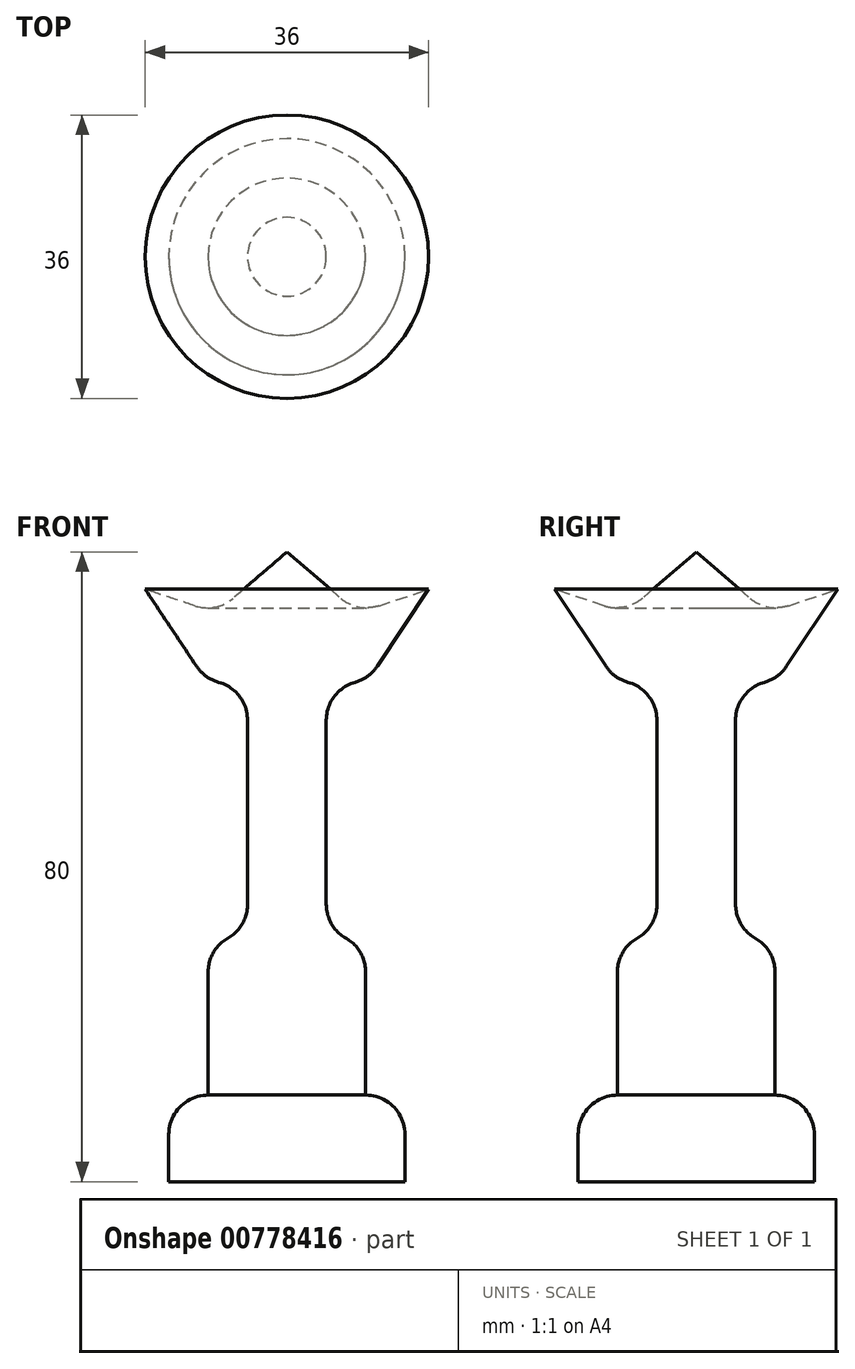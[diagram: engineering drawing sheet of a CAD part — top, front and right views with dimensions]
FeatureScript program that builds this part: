
annotation { "Feature Type Name" : "Feature", "Feature Type Description" : "" }
export const myFeature = defineFeature(function(context is Context, id is Id, definition is map)
    precondition{}
    {
        {
            var Q0;
            Q0=qCreatedBy(makeId("Front.planeOp"),FACE);
            var sketch = newSketch(context, id + "F0", { "sketchPlane" : qUnion([Q0])});
            skLineSegment(sketch, "E0", {"start": v(0, -7.82) * mm, "end": v(0, 61.44) * mm});
            skLineSegment(sketch, "E1", {"start": v(5, 55.44) * mm, "end": v(10, 55.44) * mm});
            skLineSegment(sketch, "E2", {"start": v(10, 55.44) * mm, "end": v(18, 67.44) * mm});
            skLineSegment(sketch, "E3", {"start": v(18, 67.44) * mm, "end": v(9, 64.44) * mm});
            skLineSegment(sketch, "E4", {"start": v(0, 61.44) * mm, "end": v(0, 55.44) * mm});
            skLineSegment(sketch, "E5", {"start": v(0, -7.82) * mm, "end": v(15, -7.82) * mm});
            skLineSegment(sketch, "E6", {"start": v(15, -7.82) * mm, "end": v(15, 3.18) * mm});
            skLineSegment(sketch, "E7", {"start": v(15, 3.18) * mm, "end": v(10, 3.18) * mm});
            skLineSegment(sketch, "E8", {"start": v(10, 3.18) * mm, "end": v(10, 23.7) * mm});
            skLineSegment(sketch, "E9", {"start": v(10, 23.7) * mm, "end": v(5, 23.7) * mm});
            skLineSegment(sketch, "E10", {"start": v(5, 23.7) * mm, "end": v(5, 55.44) * mm});
            skPoint(sketch, "E11.orphan", {"position": v(0, 23.7) * mm});
            skPoint(sketch, "E12.orphan", {"position": v(0, 3.18) * mm});
            skPoint(sketch, "E13.orphan", {"position": v(0, 72.18) * mm});
            skLineSegment(sketch, "E14", {"start": v(0, 61.44) * mm, "end": v(0, 72.18) * mm});
            skLineSegment(sketch, "E15", {"start": v(0, 72.18) * mm, "end": v(9, 64.44) * mm});
            skSolve(sketch);
        }
        {
            var Q0;
            Q0=makeQuery(id+"F0.imprint","IMPRINT",FACE,{"disambiguationData":[TD([[makeQuery(id+"F0.imprint","IMPRINT",EDGE,{"derivedFrom":sQuery(id+"F0.wireOp",EDGE,"E0")}),-1.0]])]});
            var Q1;
            Q1=sQuery(id+"F0.wireOp",EDGE,"E0");
            revolve(context, id + "F1", {"surfaceOperationType" : NewSurfaceOperationType.NEW, "entities" : qUnion([Q0]), "axis" : qUnion([Q1]), "revolveType" : RevolveType.FULL});
        }
        {
            var Q0;
            Q0=makeQuery(id+"F1.opRevolve","SWEPT_EDGE",EDGE,{"disambiguationData":[OSD([sQuery(id+"F0.wireOp",EDGE,"E8"),sQuery(id+"F0.wireOp",EDGE,"E9")])]});
            fillet(context, id + "F2", {"entities" : qUnion([Q0]), "radius" : 4.83 * mm, "tangentPropagation" : true, "allowEdgeOverflow" : false});
        }
        {
            var Q0;
            Q0=makeQuery(id+"F1.opRevolve","SWEPT_EDGE",EDGE,{"disambiguationData":[OSD([sQuery(id+"F0.wireOp",EDGE,"E6"),sQuery(id+"F0.wireOp",EDGE,"E7")])]});
            fillet(context, id + "F3", {"entities" : qUnion([Q0]), "radius" : 5 * mm, "tangentPropagation" : true, "allowEdgeOverflow" : false});
        }
        {
            var Q0;
            Q0=makeQuery(id+"F1.opRevolve","SWEPT_EDGE",EDGE,{"disambiguationData":[OSD([sQuery(id+"F0.wireOp",EDGE,"E9"),sQuery(id+"F0.wireOp",EDGE,"E10")])]});
            fillet(context, id + "F4", {"entities" : qUnion([Q0]), "radius" : 5 * mm, "tangentPropagation" : true, "allowEdgeOverflow" : false});
        }
        {
            var Q0;
            Q0=makeQuery(id+"F1.opRevolve","SWEPT_EDGE",EDGE,{"disambiguationData":[OSD([sQuery(id+"F0.wireOp",EDGE,"E1"),sQuery(id+"F0.wireOp",EDGE,"E2")])]});
            fillet(context, id + "F5", {"entities" : qUnion([Q0]), "radius" : 5 * mm, "tangentPropagation" : true, "allowEdgeOverflow" : false});
        }
        {
            var Q0;
            Q0=makeQuery(id+"F1.opRevolve","SWEPT_EDGE",EDGE,{"disambiguationData":[OSD([sQuery(id+"F0.wireOp",EDGE,"E3"),sQuery(id+"F0.wireOp",EDGE,"E15")])]});
            fillet(context, id + "F6", {"entities" : qUnion([Q0]), "radius" : 5 * mm, "tangentPropagation" : true, "allowEdgeOverflow" : false});
        }
        {
            var Q0;
            Q0=makeQuery(id+"F1.opRevolve","SWEPT_EDGE",EDGE,{"disambiguationData":[OSD([sQuery(id+"F0.wireOp",EDGE,"E1"),sQuery(id+"F0.wireOp",EDGE,"E10")])]});
            fillet(context, id + "F7", {"entities" : qUnion([Q0]), "radius" : 5 * mm, "tangentPropagation" : true, "allowEdgeOverflow" : false});
        }
    });
